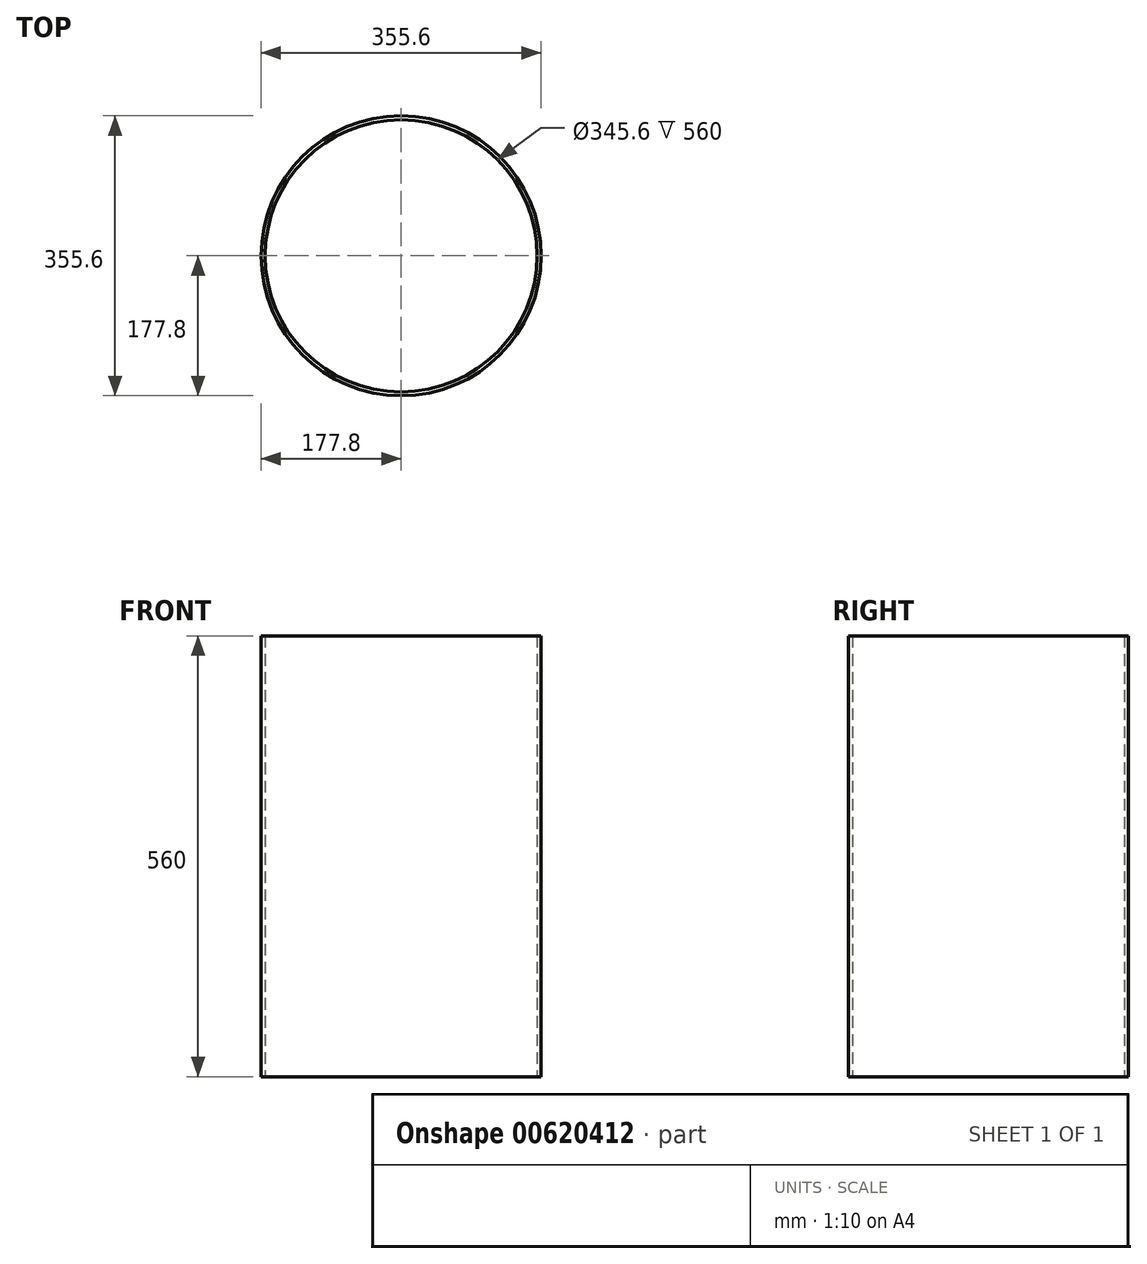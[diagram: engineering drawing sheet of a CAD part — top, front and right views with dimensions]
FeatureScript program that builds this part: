
annotation { "Feature Type Name" : "Feature", "Feature Type Description" : "" }
export const myFeature = defineFeature(function(context is Context, id is Id, definition is map)
    precondition{}
    {
        {
            var Q0;
            Q0=qCreatedBy(makeId("Top.planeOp"),FACE);
            var sketch = newSketch(context, id + "F0", { "sketchPlane" : qUnion([Q0])});
            skCircle(sketch, "E0", {"center": v(0, 0) * mm, "radius": 177.8 * mm});
            skCircle(sketch, "E1.0", {"center": v(0, 0) * mm, "radius": 172.8 * mm});
            skSolve(sketch);
        }
        {
            var Q0;
            Q0=makeQuery(id+"F0.imprint","IMPRINT",FACE,{"disambiguationData":[TD([[makeQuery(id+"F0.imprint","IMPRINT",EDGE,{"derivedFrom":sQuery(id+"F0.wireOp",EDGE,"E0")}),1.0]])]});
            extrude(context, id + "F1", {"entities" : qUnion([Q0]), "depth" : 560 * mm, "offsetDistance" : 25 * mm});
        }
    });
